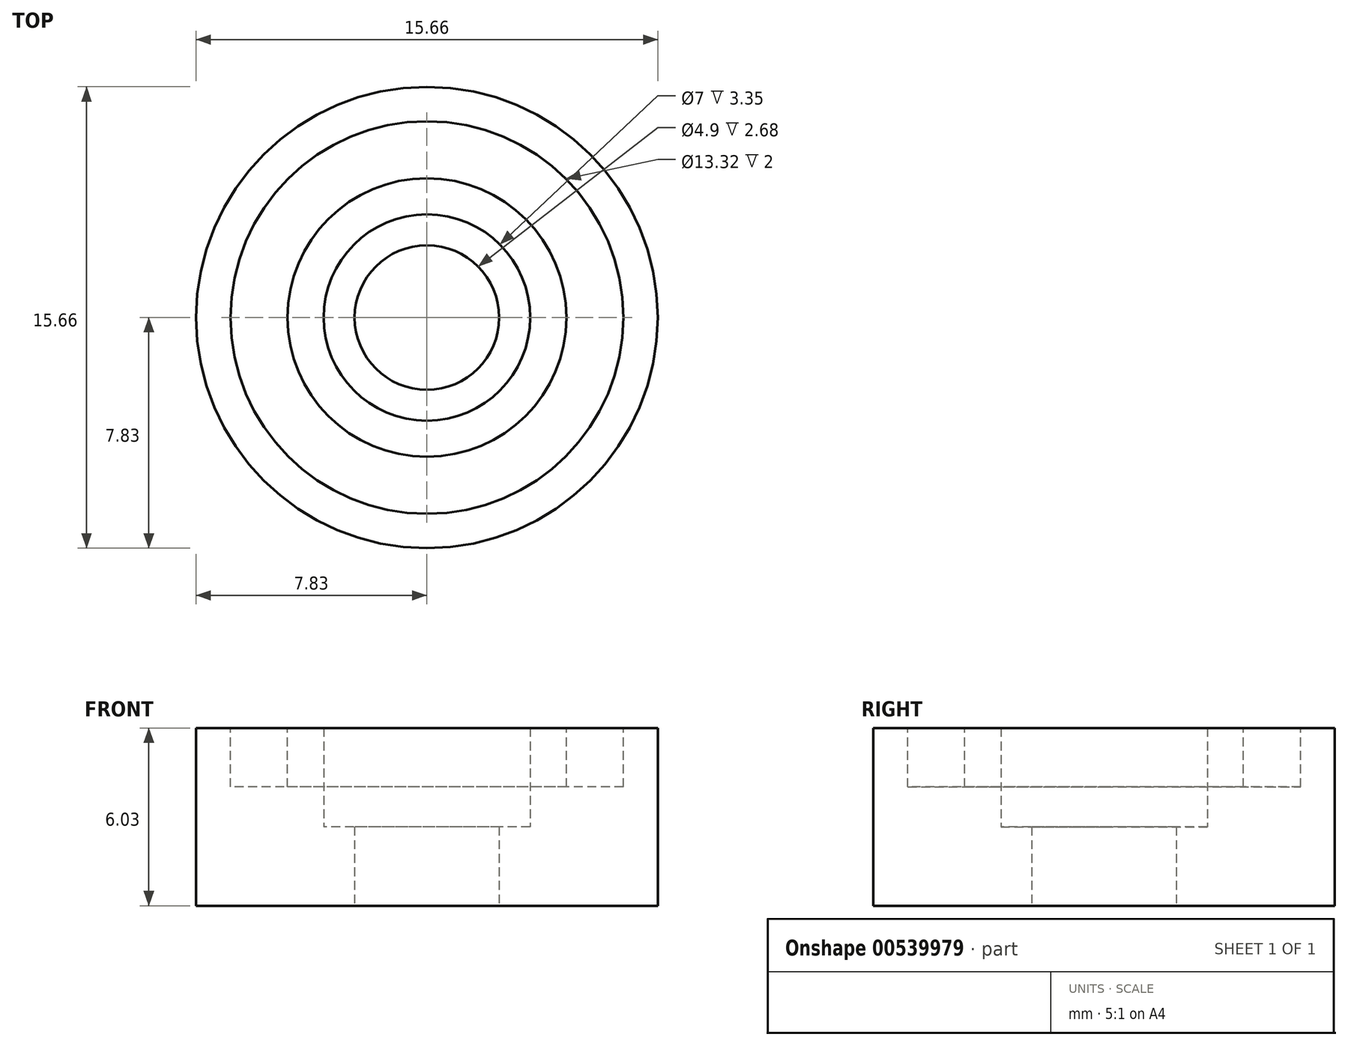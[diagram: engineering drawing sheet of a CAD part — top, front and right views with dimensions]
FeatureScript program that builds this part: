
annotation { "Feature Type Name" : "Feature", "Feature Type Description" : "" }
export const myFeature = defineFeature(function(context is Context, id is Id, definition is map)
    precondition{}
    {
        {
            var Q0;
            Q0=qCreatedBy(makeId("Top.planeOp"),FACE);
            var sketch = newSketch(context, id + "F0", { "sketchPlane" : qUnion([Q0])});
            skCircle(sketch, "E0", {"center": v(0, 0) * mm, "radius": 7.83 * mm});
            skCircle(sketch, "E1", {"center": v(0, 0) * mm, "radius": 2.45 * mm});
            skCircle(sketch, "E2", {"center": v(0, 0) * mm, "radius": 3.5 * mm});
            skSolve(sketch);
        }
        {
            var Q0;
            Q0=makeQuery(id+"F0.imprint","IMPRINT",FACE,{"disambiguationData":[TD([[makeQuery(id+"F0.imprint","IMPRINT",EDGE,{"derivedFrom":sQuery(id+"F0.wireOp",EDGE,"E0")}),1.0]])]});
            extrude(context, id + "F1", {"entities" : qUnion([Q0]), "depth" : 6.03 * mm, "offsetDistance" : 25.4 * mm});
        }
        {
            var Q0;
            Q0=makeQuery(id+"F0.imprint","IMPRINT",FACE,{"disambiguationData":[TD([[makeQuery(id+"F0.imprint","IMPRINT",EDGE,{"derivedFrom":sQuery(id+"F0.wireOp",EDGE,"E1")}),-1.0]])]});
            extrude(context, id + "F2", {"entities" : qUnion([Q0]), "operationType" : NewBodyOperationType.ADD, "depth" : 2.68 * mm, "offsetDistance" : 25.4 * mm});
        }
        {
            var Q0;
            Q0=makeQuery(id+"F1.opExtrude","CAP_FACE",FACE,{"disambiguationData":[OSD([sQuery(id+"F0.wireOp",EDGE,"E0"),sQuery(id+"F0.wireOp",EDGE,"E2")])],"isStart":false});
            var sketch = newSketch(context, id + "F3", { "sketchPlane" : qUnion([Q0])});
            skCircle(sketch, "E3", {"center": v(0, 0) * mm, "radius": 4.73 * mm});
            skCircle(sketch, "E4", {"center": v(0, 0) * mm, "radius": 6.66 * mm});
            skSolve(sketch);
        }
        {
            var Q0;
            Q0=makeQuery(id+"F3.imprint","IMPRINT",FACE,{"disambiguationData":[TD([[makeQuery(id+"F3.imprint","IMPRINT",EDGE,{"derivedFrom":sQuery(id+"F3.wireOp",EDGE,"E3")}),-1.0]])]});
            extrude(context, id + "F4", {"entities" : qUnion([Q0]), "operationType" : NewBodyOperationType.REMOVE, "oppositeDirection" : true, "depth" : 2 * mm, "offsetDistance" : 25.4 * mm});
        }
    });
